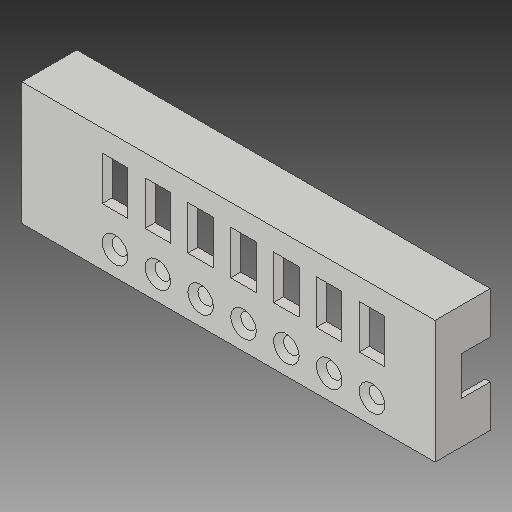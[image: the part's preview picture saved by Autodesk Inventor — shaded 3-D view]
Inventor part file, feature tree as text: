
AUTODESK INVENTOR PART (.ipt)
format: ipt  version: 2019 (Build 230136000, 136)  size: 214,528 bytes
history: native  units: mm
features: reference x5, extrude x4, sketch x4, other x3, chamfer x1
ambient origin geometry x8: Origin, YZ Plane, XZ Plane, XY Plane, X Axis, Y Axis, Z Axis, Center Point
bodies: Solid1 (feature_tree)
feature tree (17):
  extrude  "Extrusion1"  Depth=2.25mm
  extrude  "Extrusion2"  Depth=2.25mm
  extrude  "Extrusion3"  Depth=2.0mm
  extrude  "Extrusion4"  Depth=2.0mm
  chamfer  "Chamfer1"  Distance=2.0mm
  sketch  "Sketch1"  dims[d0=2.25mm d1=2.25mm]
  reference  "Reference1"
  reference  "Reference2"
  sketch  "Sketch2"  dims[d2=2.25mm d3=2.25mm]
  sketch  "Sketch3"  dims[d4=2.0mm d5=0.0mm d6=2.0mm]
  reference  "Reference3"
  reference  "Reference4"
  sketch  "Sketch4"  dims[d7=2.0mm d8=2.0mm d9=2.0mm d10=20.0mm d11=0.0mm d12=1.0mm d13=1.0mm d14=20.0mm d15=0.0mm d16=1.0mm d17=1.0mm d19=1.0mm d20=20.0mm d21=0.0mm d22=2.0mm d23=2.0mm d24=45.0deg]
  reference  "Reference5"
  parser-record x1  (decoder bookkeeping rows leaked as tree rows — omitted from the tree; the rows remain in map.json)
  other  "Assembly.iam"
  other  "hub_dummy:1"
note: 1 file-system path scrubbed to <path> (originals preserved in map.json)
